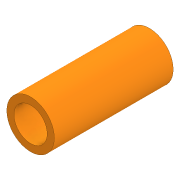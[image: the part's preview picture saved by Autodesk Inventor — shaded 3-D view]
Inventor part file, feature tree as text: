
AUTODESK INVENTOR PART (.ipt)
format: ipt  version: 2020 (Build 240168000, 168)  size: 81,920 bytes
history: native  units: in
note: dims shown in document units (in); Inventor stores cm internally (conversion verified against a paired STEP export)
features: extrude x1, sketch x1
ambient origin geometry x8: Origin, YZ Plane, XZ Plane, XY Plane, X Axis, Y Axis, Z Axis, Center Point
bodies: Solid1 (feature_tree)
feature tree (2):
  extrude  "Extrusion1"  Depth=1.9685in
  sketch  "Sketch1"  dims[d0=0.7874in d1=0.5512in d2=1.9685in d3=0.0in]
